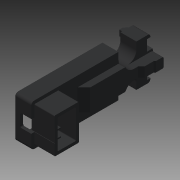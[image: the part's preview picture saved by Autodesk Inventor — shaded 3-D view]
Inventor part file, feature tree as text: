
AUTODESK INVENTOR PART (.ipt)
format: ipt  version: 2018 (Build 220112000, 112)  size: 246,272 bytes
history: native  units: mm
features: extrude x14, other x14, sketch x14
ambient origin geometry x8: Origin, YZ Plane, XZ Plane, XY Plane, X Axis, Y Axis, Z Axis, Center Point
bodies: Solid1 (feature_tree)
feature tree (42):
  extrude  "Extrusion1"  Depth=8.45mm TaperAngle=0.0deg
  extrude  "Extrusion2"  Depth=8.45mm TaperAngle=0.0deg
  extrude  "Extrusion3"  Depth=2.5mm TaperAngle=0.0deg
  extrude  "Extrusion4"  Depth=10.0mm TaperAngle=0.0deg
  extrude  "Extrusion5"  Depth=7.2mm TaperAngle=0.0deg
  extrude  "Extrusion6"  Depth=1.85mm TaperAngle=0.0deg
  extrude  "Extrusion7"  Depth=0.85mm TaperAngle=0.0deg
  extrude  "Extrusion8"  [1 undecoded]
  extrude  "Extrusion9"  [1 undecoded]
  extrude  "Extrusion10"  [1 undecoded]
  extrude  "Extrusion11"  [1 undecoded]
  extrude  "Extrusion12"  [1 undecoded]
  extrude  "Extrusion13"  [1 undecoded]
  extrude  "Extrusion14"  [1 undecoded]
  other  "NEBV_XY"
  other  "NEBV_YZ"
  other  "NEBV_ZX"
  other  "NEBV_X"
  other  "NEBV_Y"
  other  "NEBV_Z"
  other  "NEBV_Center"
  other  "VAVE_XY"
  other  "VAVE_YZ"
  other  "VAVE_ZX"
  other  "VAVE_X"
  other  "VAVE_Y"
  other  "VAVE_Z"
  other  "VAVE_Center"
  sketch  "Sketch_1"  dims[d0=8.45mm d1=0.0mm d2=8.45mm d3=0.0mm]
  sketch  "Sketch_2"  dims[d4=8.45mm d5=0.0mm d6=8.45mm d7=0.0mm]
  sketch  "Sketch_3"  dims[d8=8.45mm d9=0.0mm d10=2.5mm d11=0.0mm]
  sketch  "Sketch_4"  dims[d12=6.0mm d13=0.0mm d14=10.0mm d15=0.0mm]
  sketch  "Sketch_5"  dims[d16=3.0mm d17=0.0mm d18=7.2mm d19=0.0mm]
  sketch  "Sketch_7"  dims[d24=30.0mm d25=0.0mm d26=0.85mm d27=0.0mm]
  sketch  "Sketch_8"
  sketch  "Sketch_6"  dims[d20=30.0mm d21=0.0mm d22=1.85mm d23=0.0mm]
  sketch  "Sketch_9"
  sketch  "Sketch_13"
  sketch  "Sketch_14"
  sketch  "Sketch_11"
  sketch  "Sketch_10"
  sketch  "Sketch_12"
note: 7 required parameter values undecoded (feature->parameter linkage not recoverable at this tier; creation-order binding heuristic only, values carry confidence <= 0.55)
